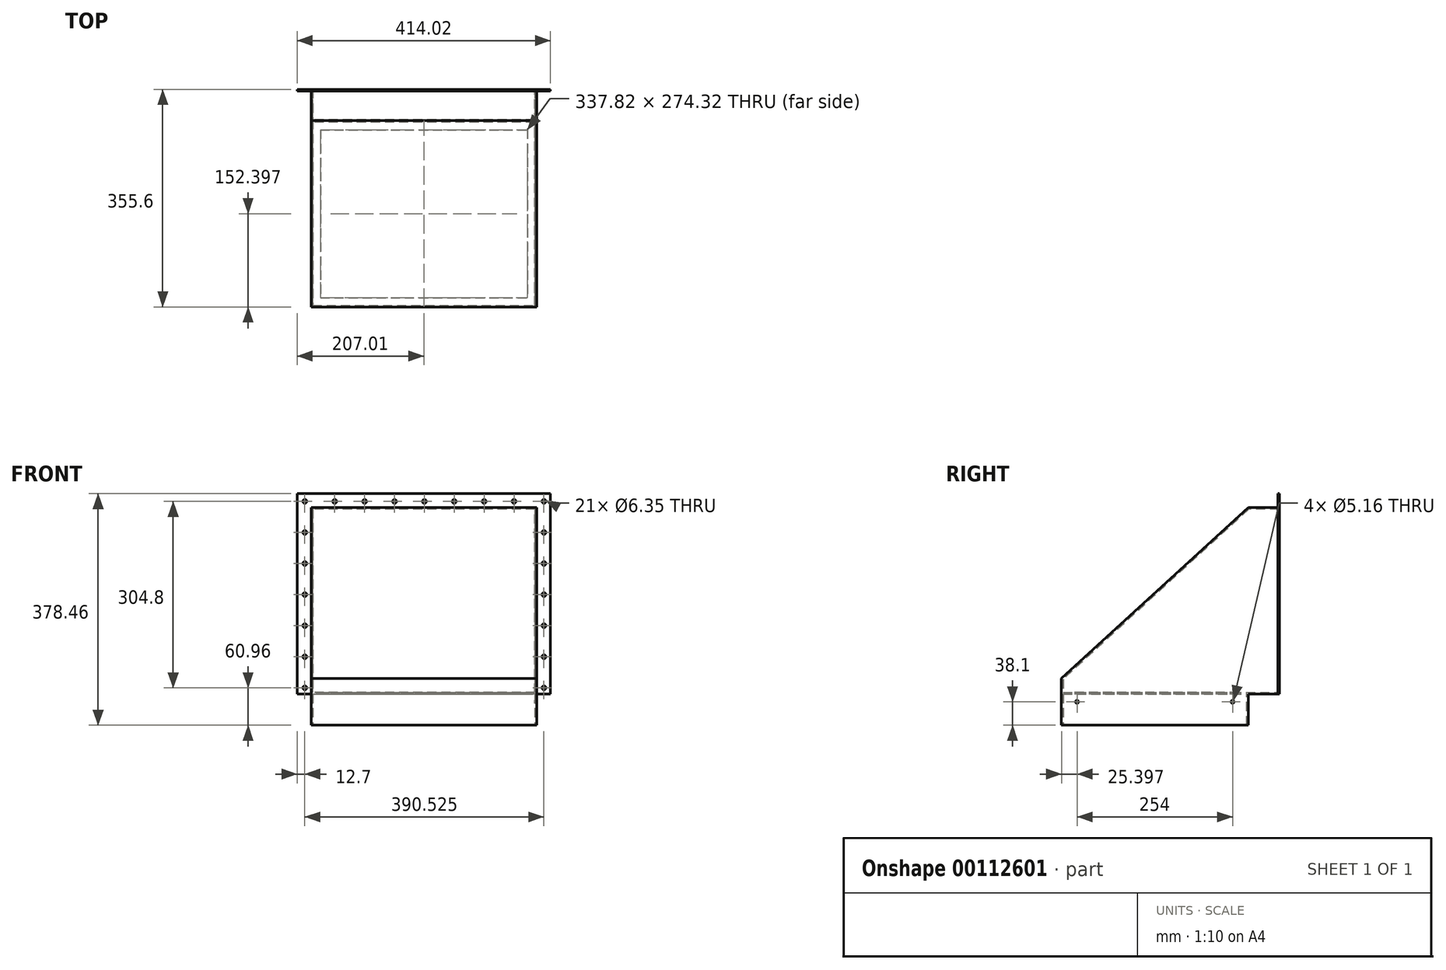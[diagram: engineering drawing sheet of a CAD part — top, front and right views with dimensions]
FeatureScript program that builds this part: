
annotation { "Feature Type Name" : "Feature", "Feature Type Description" : "" }
export const myFeature = defineFeature(function(context is Context, id is Id, definition is map)
    precondition{}
    {
        {
            var Q0;
            Q0=qCreatedBy(makeId("Right.planeOp"),FACE);
            var sketch = newSketch(context, id + "F0", { "sketchPlane" : qUnion([Q0])});
            skLineSegment(sketch, "E0", {"start": v(98.6, 50.8) * mm, "end": v(98.6, 355.6) * mm});
            skLineSegment(sketch, "E1", {"start": v(98.6, 355.6) * mm, "end": v(47.8, 355.6) * mm});
            skLineSegment(sketch, "E2", {"start": v(47.8, 355.6) * mm, "end": v(-257, 76.2) * mm});
            skLineSegment(sketch, "E3", {"start": v(-257, 76.2) * mm, "end": v(-257, 0) * mm});
            skLineSegment(sketch, "E4", {"start": v(-257, 0) * mm, "end": v(47.8, 0) * mm});
            skLineSegment(sketch, "E5", {"start": v(47.8, 0) * mm, "end": v(47.8, 50.8) * mm});
            skLineSegment(sketch, "E6", {"start": v(47.8, 50.8) * mm, "end": v(98.6, 50.8) * mm});
            skSolve(sketch);
        }
        {
            var Q0;
            Q0 = qSketchRegion(id + "F0", true);
            extrude(context, id + "F1", {"entities" : qUnion([Q0]), "endBound" : BoundingType.SYMMETRIC, "depth" : 368.3 * mm});
        }
        {
            var Q0;
            Q0=makeQuery(id+"F1.opExtrude","SWEPT_FACE",FACE,{"disambiguationData":[OSD([sQuery(id+"F0.wireOp",EDGE,"E0")])]});
            var Q1;
            Q1=makeQuery(id+"F1.opExtrude","SWEPT_FACE",FACE,{"disambiguationData":[OSD([sQuery(id+"F0.wireOp",EDGE,"E4")])]});
            shell(context, id + "F2", {"entities" : qUnion([Q0, Q1]), "thickness" : 2.54 * mm});
        }
        {
            var Q0;
            Q0=makeQuery(id+"F1.opExtrude","SWEPT_FACE",FACE,{"disambiguationData":[OSD([sQuery(id+"F0.wireOp",EDGE,"E0")])]});
            var sketch = newSketch(context, id + "F3", { "sketchPlane" : qUnion([Q0])});
            skLineSegment(sketch, "E7", {"start": v(-181.6, 50.8) * mm, "end": v(-207, 50.8) * mm});
            skLineSegment(sketch, "E8", {"start": v(-207, 50.8) * mm, "end": v(-207, 378.46) * mm});
            skLineSegment(sketch, "E9", {"start": v(-207, 378.46) * mm, "end": v(207, 378.46) * mm});
            skLineSegment(sketch, "E10", {"start": v(207, 378.46) * mm, "end": v(207, 50.8) * mm});
            skLineSegment(sketch, "E11", {"start": v(207, 50.8) * mm, "end": v(181.6, 50.8) * mm});
            skLineSegment(sketch, "E12", {"start": v(181.6, 50.8) * mm, "end": v(181.6, 353.06) * mm});
            skLineSegment(sketch, "E13", {"start": v(181.6, 353.06) * mm, "end": v(-181.6, 353.06) * mm});
            skLineSegment(sketch, "E14", {"start": v(-181.6, 353.06) * mm, "end": v(-181.6, 50.8) * mm});
            skSolve(sketch);
        }
        {
            var Q0;
            Q0 = qSketchRegion(id + "F3", true);
            extrude(context, id + "F4", {"entities" : qUnion([Q0]), "operationType" : NewBodyOperationType.ADD, "oppositeDirection" : true, "depth" : 2.54 * mm});
        }
        {
            var Q0;
            Q0=makeQuery(id+"F2.opShell","OFFSET_FACE",FACE,{"disambiguationData":[OSD([sQuery(id+"F0.wireOp",EDGE,"E6")])]});
            var sketch = newSketch(context, id + "F5", { "sketchPlane" : qUnion([Q0])});
            skLineSegment(sketch, "E15.bottom", {"start": v(-181.61, 45.27) * mm, "end": v(181.6, 45.27) * mm});
            skLineSegment(sketch, "E15.top", {"start": v(-181.6, -254.45) * mm, "end": v(181.61, -254.45) * mm});
            skLineSegment(sketch, "E15.left", {"start": v(-181.6, -254.45) * mm, "end": v(-181.61, 45.27) * mm});
            skLineSegment(sketch, "E15.right", {"start": v(181.61, -254.45) * mm, "end": v(181.6, 45.27) * mm});
            skLineSegment(sketch, "E16.bottom", {"start": v(-168.91, -241.75) * mm, "end": v(168.91, -241.75) * mm});
            skLineSegment(sketch, "E16.top", {"start": v(-168.91, 32.57) * mm, "end": v(168.9, 32.57) * mm});
            skLineSegment(sketch, "E16.left", {"start": v(-168.9, 32.57) * mm, "end": v(-168.9, -241.75) * mm});
            skLineSegment(sketch, "E16.right", {"start": v(168.91, 32.57) * mm, "end": v(168.91, -241.75) * mm});
            skSolve(sketch);
        }
        {
            var Q0;
            Q0 = qSketchRegion(id + "F5", true);
            extrude(context, id + "F6", {"entities" : qUnion([Q0]), "operationType" : NewBodyOperationType.ADD, "oppositeDirection" : true, "depth" : 2.54 * mm});
        }
        {
            var Q0;
            Q0=makeQuery(id+"F1.opExtrude","CAP_FACE",FACE,{"disambiguationData":[OSD([sQuery(id+"F0.wireOp",EDGE,"E0"),sQuery(id+"F0.wireOp",EDGE,"E1"),sQuery(id+"F0.wireOp",EDGE,"E2"),sQuery(id+"F0.wireOp",EDGE,"E3"),sQuery(id+"F0.wireOp",EDGE,"E4"),sQuery(id+"F0.wireOp",EDGE,"E5"),sQuery(id+"F0.wireOp",EDGE,"E6")])],"isStart":true});
            var sketch = newSketch(context, id + "F7", { "sketchPlane" : qUnion([Q0])});
            skCircle(sketch, "E17", {"center": v(-22.4, 38.1) * mm, "radius": 2.58 * mm});
            skCircle(sketch, "E18", {"center": v(231.6, 38.1) * mm, "radius": 2.58 * mm});
            skSolve(sketch);
        }
        {
            var Q0;
            Q0 = qSketchRegion(id + "F7", true);
            extrude(context, id + "F8", {"entities" : qUnion([Q0]), "operationType" : NewBodyOperationType.REMOVE, "endBound" : BoundingType.THROUGH_ALL, "oppositeDirection" : true, "depth" : 25.4 * mm});
        }
        {
            var Q0;
            Q0=makeQuery(id+"F4.opExtrude","CAP_FACE",FACE,{"disambiguationData":[OSD([sQuery(id+"F3.wireOp",EDGE,"E7"),sQuery(id+"F3.wireOp",EDGE,"E8"),sQuery(id+"F3.wireOp",EDGE,"E9"),sQuery(id+"F3.wireOp",EDGE,"E10"),sQuery(id+"F3.wireOp",EDGE,"E11"),sQuery(id+"F3.wireOp",EDGE,"E12"),sQuery(id+"F3.wireOp",EDGE,"E13"),sQuery(id+"F3.wireOp",EDGE,"E14")])],"isStart":false});
            var sketch = newSketch(context, id + "F9", { "sketchPlane" : qUnion([Q0])});
            skCircle(sketch, "E19", {"center": v(-194.3, 365.76) * mm, "radius": 3.18 * mm});
            skCircle(sketch, "E20.0.1.0", {"center": v(-194.3, 314.96) * mm, "radius": 3.18 * mm});
            skCircle(sketch, "E20.0.2.0", {"center": v(-194.3, 264.16) * mm, "radius": 3.18 * mm});
            skCircle(sketch, "E20.0.3.0", {"center": v(-194.3, 213.36) * mm, "radius": 3.18 * mm});
            skCircle(sketch, "E20.0.4.0", {"center": v(-194.3, 162.56) * mm, "radius": 3.18 * mm});
            skCircle(sketch, "E20.0.5.0", {"center": v(-194.3, 111.76) * mm, "radius": 3.18 * mm});
            skCircle(sketch, "E20.0.6.0", {"center": v(-194.3, 60.96) * mm, "radius": 3.18 * mm});
            skCircle(sketch, "E20.1.0.0", {"center": v(196.22, 365.76) * mm, "radius": 3.18 * mm});
            skCircle(sketch, "E20.1.1.0", {"center": v(196.22, 314.96) * mm, "radius": 3.18 * mm});
            skCircle(sketch, "E20.1.2.0", {"center": v(196.22, 264.16) * mm, "radius": 3.18 * mm});
            skCircle(sketch, "E20.1.3.0", {"center": v(196.22, 213.36) * mm, "radius": 3.18 * mm});
            skCircle(sketch, "E20.1.4.0", {"center": v(196.22, 162.56) * mm, "radius": 3.18 * mm});
            skCircle(sketch, "E20.1.5.0", {"center": v(196.22, 111.76) * mm, "radius": 3.18 * mm});
            skCircle(sketch, "E20.1.6.0", {"center": v(196.22, 60.96) * mm, "radius": 3.18 * mm});
            skLineSegment(sketch, "E20.direction1", {"start": v(-194.3, 365.76) * mm, "end": v(196.22, 365.76) * mm, "construction": true});
            skLineSegment(sketch, "E20.direction2", {"start": v(-194.3, 365.76) * mm, "end": v(-194.3, 314.96) * mm, "construction": true});
            skCircle(sketch, "E21.1.0.0", {"center": v(147.4, 365.76) * mm, "radius": 3.18 * mm});
            skCircle(sketch, "E21.2.0.0", {"center": v(98.58, 365.76) * mm, "radius": 3.18 * mm});
            skCircle(sketch, "E21.3.0.0", {"center": v(49.76, 365.76) * mm, "radius": 3.18 * mm});
            skCircle(sketch, "E21.4.0.0", {"center": v(0.94, 365.76) * mm, "radius": 3.18 * mm});
            skCircle(sketch, "E21.5.0.0", {"center": v(-47.88, 365.76) * mm, "radius": 3.18 * mm});
            skCircle(sketch, "E21.6.0.0", {"center": v(-96.7, 365.76) * mm, "radius": 3.18 * mm});
            skCircle(sketch, "E21.7.0.0", {"center": v(-145.52, 365.76) * mm, "radius": 3.18 * mm});
            skLineSegment(sketch, "E21.direction1", {"start": v(196.22, 365.76) * mm, "end": v(147.4, 365.76) * mm, "construction": true});
            skSolve(sketch);
        }
        {
            var Q0;
            Q0 = qSketchRegion(id + "F9", true);
            extrude(context, id + "F10", {"entities" : qUnion([Q0]), "operationType" : NewBodyOperationType.REMOVE, "endBound" : BoundingType.THROUGH_ALL, "oppositeDirection" : true, "depth" : 25.4 * mm});
        }
    });
